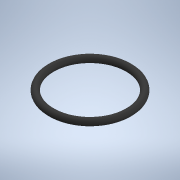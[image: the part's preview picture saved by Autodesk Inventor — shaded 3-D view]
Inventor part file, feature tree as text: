
AUTODESK INVENTOR PART (.ipt)
format: ipt  version: 2020.3 (Build 243373000, 373)  size: 124,416 bytes
history: native  units: mm
features: revolve x1, sketch x1
ambient origin geometry x8: Origin, YZ Plane, XZ Plane, XY Plane, X Axis, Y Axis, Z Axis, Center Point
bodies: Solid1 (feature_tree)
feature tree (2):
  revolve  "Revolution1"  [1 undecoded]
  sketch  "Sketch1"  dims[d0=1.78mm d1=10.39mm d2=90.0deg]
note: 1 required parameter value undecoded (feature->parameter linkage not recoverable at this tier; creation-order binding heuristic only, values carry confidence <= 0.55)
